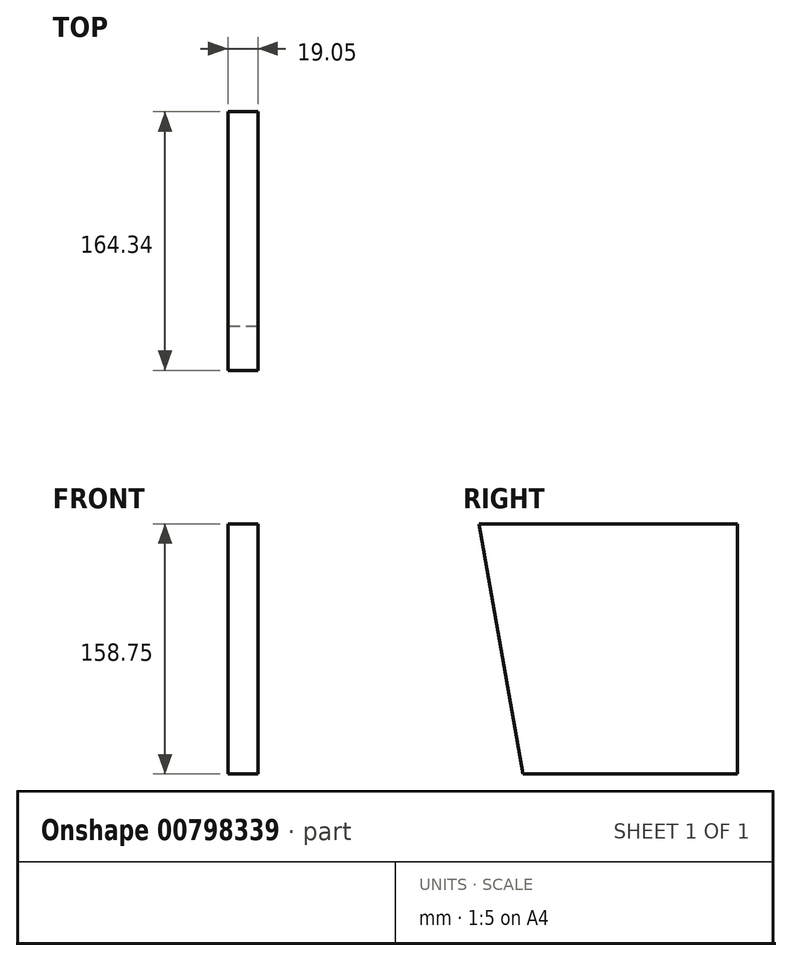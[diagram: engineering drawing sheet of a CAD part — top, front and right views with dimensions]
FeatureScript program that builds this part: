
annotation { "Feature Type Name" : "Feature", "Feature Type Description" : "" }
export const myFeature = defineFeature(function(context is Context, id is Id, definition is map)
    precondition{}
    {
        {
            var Q0;
            Q0=qCreatedBy(makeId("Right.planeOp"),FACE);
            var sketch = newSketch(context, id + "F0", { "sketchPlane" : qUnion([Q0])});
            skLineSegment(sketch, "E0", {"start": v(0, 0) * mm, "end": v(136.35, 0) * mm});
            skLineSegment(sketch, "E1", {"start": v(136.35, 0) * mm, "end": v(136.35, 158.75) * mm});
            skLineSegment(sketch, "E2", {"start": v(136.35, 158.75) * mm, "end": v(-28, 158.75) * mm});
            skLineSegment(sketch, "E3", {"start": v(-28, 158.75) * mm, "end": v(0, 0) * mm});
            skSolve(sketch);
        }
        {
            var Q0;
            Q0 = qSketchRegion(id + "F0", true);
            extrude(context, id + "F1", {"entities" : qUnion([Q0]), "depth" : 19.05 * mm, "offsetDistance" : 25.4 * mm});
        }
    });
